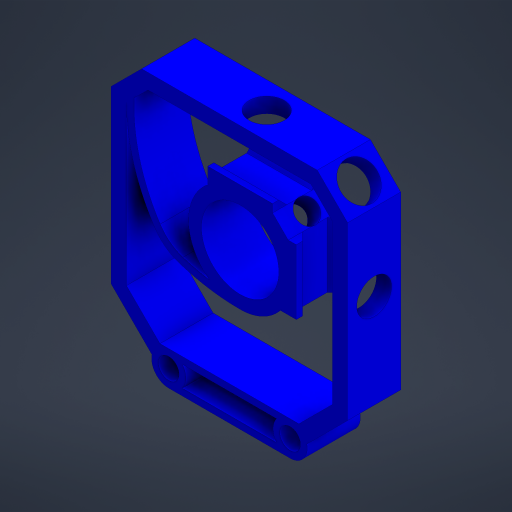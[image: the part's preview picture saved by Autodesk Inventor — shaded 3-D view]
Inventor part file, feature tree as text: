
AUTODESK INVENTOR PART (.ipt)
format: ipt  version: 2023.4 (Build 274418000, 418)  size: 513,536 bytes
history: native  units: mm
features: extrude x6, projected_geometry x4, reference x4, other x3, plane x1, mirror x1, sketch x1
ambient origin geometry x8: Origin, YZ Plane, XZ Plane, XY Plane, X Axis, Y Axis, Z Axis, Center Point
bodies: Solid1 (feature_tree)
feature tree (20):
  extrude  "Extrusion1"  TaperAngle=45.0deg  [1 undecoded]
  extrude  "Extrusion2"  Depth=10.0mm
  extrude  "Extrusion3"  Depth=10.0mm
  extrude  "Extrusion4"  Depth=10.0mm
  plane  "Work Plane1"
  mirror  "Mirror1"
  extrude  "Extrusion5"  Depth=10.0mm
  extrude  "Extrusion6"  Depth=10.0mm
  sketch  "Sketch1"  dims[d2=2.5mm d3=45.0deg d4=12.75mm d5=0.675mm d6=2.125mm d7=0.5mm d8=10.675mm d9=2.5mm d10=0.625mm d11=5.0mm d12=135.0deg d13=3.0mm d14=2.0mm d15=2.0mm d16=38.935534mm d17=38.935534mm d18=9.25mm d19=9.25mm d20=9.25mm d21=9.25mm d22=5.0mm d23=5.0mm d24=5.0mm d25=5.0mm d26=2.5mm d28=8.75mm d29=0.0mm d30=0.875mm d31=0.875mm d32=0.0mm d33=5.75mm d34=10.0mm d35=0.0mm d36=1.0mm d37=135.0deg d38=10.0mm d39=0.0mm d40=3.75mm d41=6.0mm d42=5.0mm d43=0.0mm d44=10.0mm d45=0.0mm d46=2.5mm d50=12.5mm d51=2.5mm d52=1.25mm d53=2.5mm d54=2.5mm d61=1.25mm d62=1.25mm d63=0.1425mm d64=0.1425mm]
  projected_geometry  "Projected Loop1"
  projected_geometry  "Projected Loop2"
  projected_geometry  "Projected Loop4"
  projected_geometry  "Projected Loop5"
  reference  "Reference4"
  reference  "Reference5"
  reference  "Reference6"
  reference  "Reference7"
  other  "<path>\Projects\Project Protocube\Protocube\CAD, STL, OBJ Files\1 CAD\Cube 1x1 V5.iam"
  other  "Cube 1x1 V5.iam"
  other  "Cube 1x1 Bottom V5 Closed Slotted:1"
note: 1 required parameter value undecoded (feature->parameter linkage not recoverable at this tier; creation-order binding heuristic only, values carry confidence <= 0.55)
note: 1 file-system path scrubbed to <path> (originals preserved in map.json)
